FCSTD DOCUMENT  (FreeCAD 1.0R39109 (Git))
Label: Mount_assembly_1inch
License: All rights reserved
LicenseURL: https://en.wikipedia.org/wiki/All_rights_reserved
objects: PartDesign::CoordinateSystem×15, App::Link×3, App::DocumentObjectGroup×2, App::FeaturePython×1, App::Part×1
note: 15 computed .brp shape members not serialized (recipe doc carries the construction recipe); baked Part::Feature solids carry a one-line shape summary decoded from their .brp
EXTERNAL_REF file=Post_4inches.FCStd obj=HoleAxis_1
EXTERNAL_REF file=Post_4inches.FCStd obj=Assembly
EXTERNAL_REF file=PostSpacer_3inches.FCStd obj=HoleAxis_1
EXTERNAL_REF file=Post_4inches.FCStd obj=HoleAxis_2
EXTERNAL_REF file=PostSpacer_3inches.FCStd obj=Assembly
EXTERNAL_REF file=PostSpacer_3inches.FCStd obj=HoleAxis_2
EXTERNAL_REF file=lens_mount_1inch.FCStd obj=HoleAxis_1
EXTERNAL_REF file=lens_mount_1inch.FCStd obj=Assembly

FEATURE [PartDesign::CoordinateSystem] LCS_Origin
  AttacherType = Attacher::AttachEngine3D
  AttachmentSupport = -> [X_Axis]
  MapMode = 2
FEATURE [App::DocumentObjectGroup] Constraints
FEATURE [App::FeaturePython] Variables  # WARN: FeaturePython — macro-defined, semantics opaque (R4)
  Type = App::PropertyContainer
FEATURE [App::DocumentObjectGroup] Configurations
FEATURE [PartDesign::CoordinateSystem] Bottom_center_6
  AttacherType = Attacher::AttachEngine3D
  Placement = pos=(0,0,0) rot=(0,0,1;0.10472rad)
FEATURE [PartDesign::CoordinateSystem] LCS_3  label="Component_center"
  AttacherType = Attacher::AttachEngine3D
  Placement = pos=(0,0,199.9) rot=(0,0,1;0rad)
FEATURE [PartDesign::CoordinateSystem] Botto_center_minus_6  label="Bottom_center_minus_6"
  AttacherType = Attacher::AttachEngine3D
  Placement = pos=(0,0,0) rot=(0,0,-1;0.10472rad)
FEATURE [PartDesign::CoordinateSystem] _5  label="Bottom_center_45"
  AttacherType = Attacher::AttachEngine3D
  Placement = pos=(0,0,0) rot=(0,0,1;0.785398rad)
FEATURE [App::Link] Post_4inches
  AttachedBy = #HoleAxis_1
  AttachedTo = Parent Assembly#LCS_Origin
  LinkPlacement = pos=(-5.3e-15,-1.07e-14,50.8) rot=(0.57735,0.57735,0.57735;2.0944rad)
  LinkedObject = -> <external Post_4inches.FCStd>#Assembly
  Placement = pos=(-5.3e-15,-1.07e-14,50.8) rot=(0.57735,0.57735,0.57735;2.0944rad)
  SolverId = Asm4EE
  expr: Placement = LCS_Origin.Placement * AttachmentOffset * Post_4inches#HoleAxis_1.Placement ^ -1
FEATURE [App::Link] PostSpacer_3inches
  AttachedBy = #HoleAxis_1
  AttachedTo = Post_4inches#HoleAxis_2
  LinkPlacement = pos=(-1.39295,-15.1208,153.495) rot=(0.57735,0.57735,0.57735;2.0944rad)
  LinkedObject = -> <external PostSpacer_3inches.FCStd>#Assembly
  Placement = pos=(-1.39295,-15.1208,153.495) rot=(0.57735,0.57735,0.57735;2.0944rad)
  SolverId = Asm4EE
  expr: Placement = Post_4inches.Placement * Post_4inches#HoleAxis_2.Placement * AttachmentOffset * PostSpacer_3inches#HoleAxis_1.Placement ^ -1
FEATURE [App::Link] lens_mount_1inch
  AttachedBy = #HoleAxis_1
  AttachedTo = PostSpacer_3inches#HoleAxis_2
  AttachmentOffset = pos=(0,0,0) rot=(0,1,0;3.14159rad)
  LinkPlacement = pos=(-5.08,2.3e-14,199.898) rot=(-0.57735,0.57735,0.57735;4.18879rad)
  LinkedObject = -> <external lens_mount_1inch.FCStd>#Assembly
  Placement = pos=(-5.08,2.3e-14,199.898) rot=(-0.57735,0.57735,0.57735;4.18879rad)
  SolverId = Asm4EE
  expr: Placement = PostSpacer_3inches.Placement * PostSpacer_3inches#HoleAxis_2.Placement * AttachmentOffset * lens_mount_1inch#HoleAxis_1.Placement ^ -1
FEATURE [PartDesign::CoordinateSystem] Bottom_center_39
  AttacherType = Attacher::AttachEngine3D
  Placement = pos=(0,0,0) rot=(0,0,1;0.680678rad)
FEATURE [PartDesign::CoordinateSystem] Bottom_center_25  label="Bottom_center_16"
  AttacherType = Attacher::AttachEngine3D
  Placement = pos=(0,0,0) rot=(0,0,1;0.279253rad)
FEATURE [PartDesign::CoordinateSystem] Bottom_center_74  label="Bottom_center_65"
  AttacherType = Attacher::AttachEngine3D
  Placement = pos=(0,0,0) rot=(0,0,1;1.13446rad)
FEATURE [PartDesign::CoordinateSystem] Bottom_center_20
  AttacherType = Attacher::AttachEngine3D
  Placement = pos=(0,0,0) rot=(0,0,1;0.349066rad)
FEATURE [PartDesign::CoordinateSystem] Bottom_center_minus_20
  AttacherType = Attacher::AttachEngine3D
  Placement = pos=(0,0,0) rot=(0,0,-1;0.349066rad)
FEATURE [PartDesign::CoordinateSystem] Bottom_center_51
  AttacherType = Attacher::AttachEngine3D
  Placement = pos=(0,0,0) rot=(0,0,1;0.890118rad)
FEATURE [PartDesign::CoordinateSystem] Bottom_center_15
  AttacherType = Attacher::AttachEngine3D
  Placement = pos=(0,0,0) rot=(0,0,1;0.261799rad)
FEATURE [PartDesign::CoordinateSystem] Bottom_center_70  label="Bottom_center_55"
  AttacherType = Attacher::AttachEngine3D
  Placement = pos=(0,0,0) rot=(0,0,1;0.959931rad)
FEATURE [PartDesign::CoordinateSystem] Bottom_center  label="Bottom_center_27"
  AttacherType = Attacher::AttachEngine3D
  Placement = pos=(0,0,0) rot=(0,0,1;0.471239rad)
FEATURE [PartDesign::CoordinateSystem] Bottom_center_67  label="Bottom_center_72"
  AttacherType = Attacher::AttachEngine3D
  Placement = pos=(0,0,0) rot=(0,0,1;1.25664rad)
FEATURE [App::Part] Assembly
  AssemblyType = Part::Link
  Group = -> [LCS_Origin,Constraints,Variables,Configurations,Bottom_center_6,LCS_3,Botto_center_minus_6,_5,Post_4inches,PostSpacer_3inches,lens_mount_1inch,Bottom_center_39,Bottom_center_25,Bottom_center_74,Bottom_center_20,Bottom_center_minus_20,Bottom_center_51,Bottom_center_15,Bottom_center_70,Bottom_center,Bottom_center_67]
  Origin = -> Origin
  Type = Assembly
